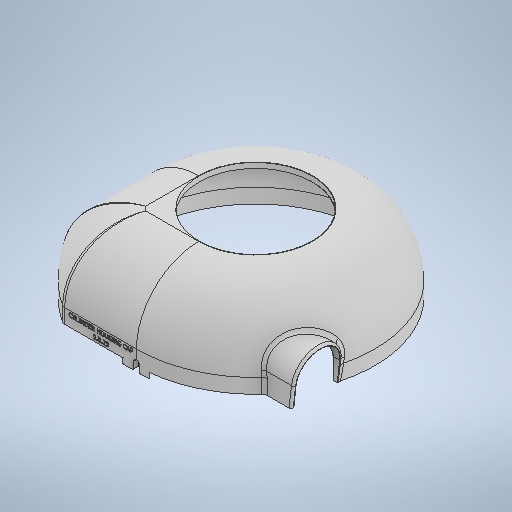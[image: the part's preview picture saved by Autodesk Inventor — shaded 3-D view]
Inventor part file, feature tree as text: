
AUTODESK INVENTOR PART (.ipt)
format: ipt  version: 2025 (Build 290162000, 162)  size: 1,138,688 bytes
history: native  units: mm
features: sketch x8, extrude x6, fillet x4, shell x1, hole x1, plane x1, other x1
ambient origin geometry x8: Origin, YZ Plane, XZ Plane, XY Plane, X Axis, Y Axis, Z Axis, Center Point
bodies: Solid1 (feature_tree)
feature tree (22):
  extrude  "Extrusion1"  Depth=60.0mm
  fillet  "THE FILLET"  Radius=5.0mm
  shell  "Shell1"  Thickness=115.0mm
  hole  "Hole1"  [1 undecoded]
  extrude  "Extrusion2"  Depth=20.0mm
  plane  "Work Plane1"
  extrude  "Hood"  Depth=116.0mm
  extrude  "Slanted Edge"  Depth=10.0mm TaperAngle=0.0deg
  fillet  "Fillet2"  Radius=10.0mm
  fillet  "Fillet4"  Radius=2.0mm
  other  "LABEL"
  extrude  "Extrusion7"  Depth=1.0mm TaperAngle=0.0deg
  extrude  "Extrusion8"  Depth=1.0mm
  fillet  "Fillet5"  Radius=5.0mm
  sketch  "Sketch1"  dims[d0=74.0mm d1=0.0mm d2=60.0mm d3=5.0mm]
  sketch  "Sketch2"  dims[d4=109.0mm d5=6.0mm d6=9.0mm d7=5.0mm d8=90.0deg d9=8.0mm d10=20.594885mm d11=115.0mm]
  sketch  "Sketch3"  dims[d13=270.0mm d14=42.0mm]
  sketch  "Sketch4"  dims[d15=53.226mm d16=20.0mm]
  sketch  "Sketch5"  dims[d17=0.0mm d18=0.0mm d19=116.0mm]
  sketch  "Sketch11"  dims[d20=47.0mm d21=10.0mm d22=0.0mm d23=10.0mm d24=0.0mm d25=2.0mm]
  sketch  "Sketch13"  dims[d27=5.0mm d35=1.0mm d36=0.0mm]
  sketch  "Sketch14"  dims[d42=15.7mm d43=7.0mm d44=5.0mm d45=0.0mm d46=5.5mm d47=7.5mm d48=0.0mm d49=0.0mm d50=1.0mm d33=0.0mm d34=0.0mm d51=0.5mm d52=0.872665mm d53=0.5mm d54=0.872665mm d55=109.0mm d56=0.375mm d57=14.3117mm d58=0.75mm d59=20.594885mm d60=0.0625mm d61=0.75mm d62=0.375mm]
note: 1 required parameter value undecoded (feature->parameter linkage not recoverable at this tier; creation-order binding heuristic only, values carry confidence <= 0.55)
